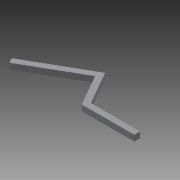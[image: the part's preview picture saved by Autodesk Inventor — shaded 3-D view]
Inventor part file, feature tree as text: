
AUTODESK INVENTOR PART (.ipt)
format: ipt  version: 2013 (Build 170138000, 138)  size: 76,288 bytes
history: native  units: in
note: dims shown in document units (in); Inventor stores cm internally (conversion verified against a paired STEP export)
features: extrude x1, sketch x1
ambient origin geometry x8: Origin, YZ Plane, XZ Plane, XY Plane, X Axis, Y Axis, Z Axis, Center Point
bodies: Solid1 (feature_tree)
feature tree (2):
  extrude  "Extrusion1"  Depth=1.0in
  sketch  "Sketch1"  dims[d0=1.0in d1=1.0in d2=1.0in d3=1.0in d4=1.0in d5=1.0in d6=1.0in d7=0.0in]
